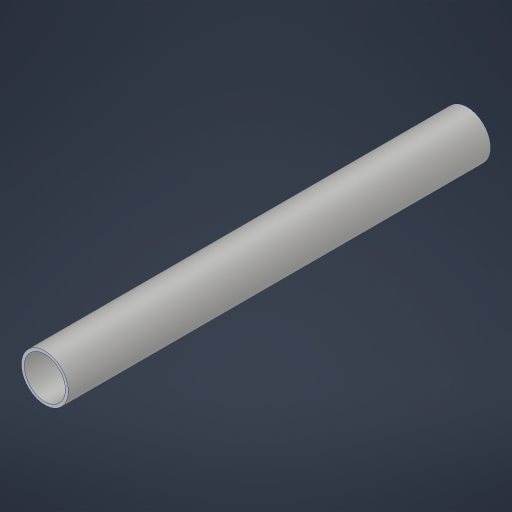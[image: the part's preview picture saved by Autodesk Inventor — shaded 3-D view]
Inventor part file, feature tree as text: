
AUTODESK INVENTOR PART (.ipt)
format: ipt  version: 2023.4 (Build 274418000, 418)  size: 171,008 bytes
history: native  units: in
note: dims shown in document units (in); Inventor stores cm internally (conversion verified against a paired STEP export)
features: extrude x1, sketch x1
ambient origin geometry x8: Origin, YZ Plane, XZ Plane, XY Plane, X Axis, Y Axis, Z Axis, Center Point
bodies: Solid1 (feature_tree)
feature tree (2):
  extrude  "Extrusion1"  Depth=18.0in
  sketch  "Sketch1"  dims[d0=2.0in d1=0.125in d2=18.0in d3=0.0in]
